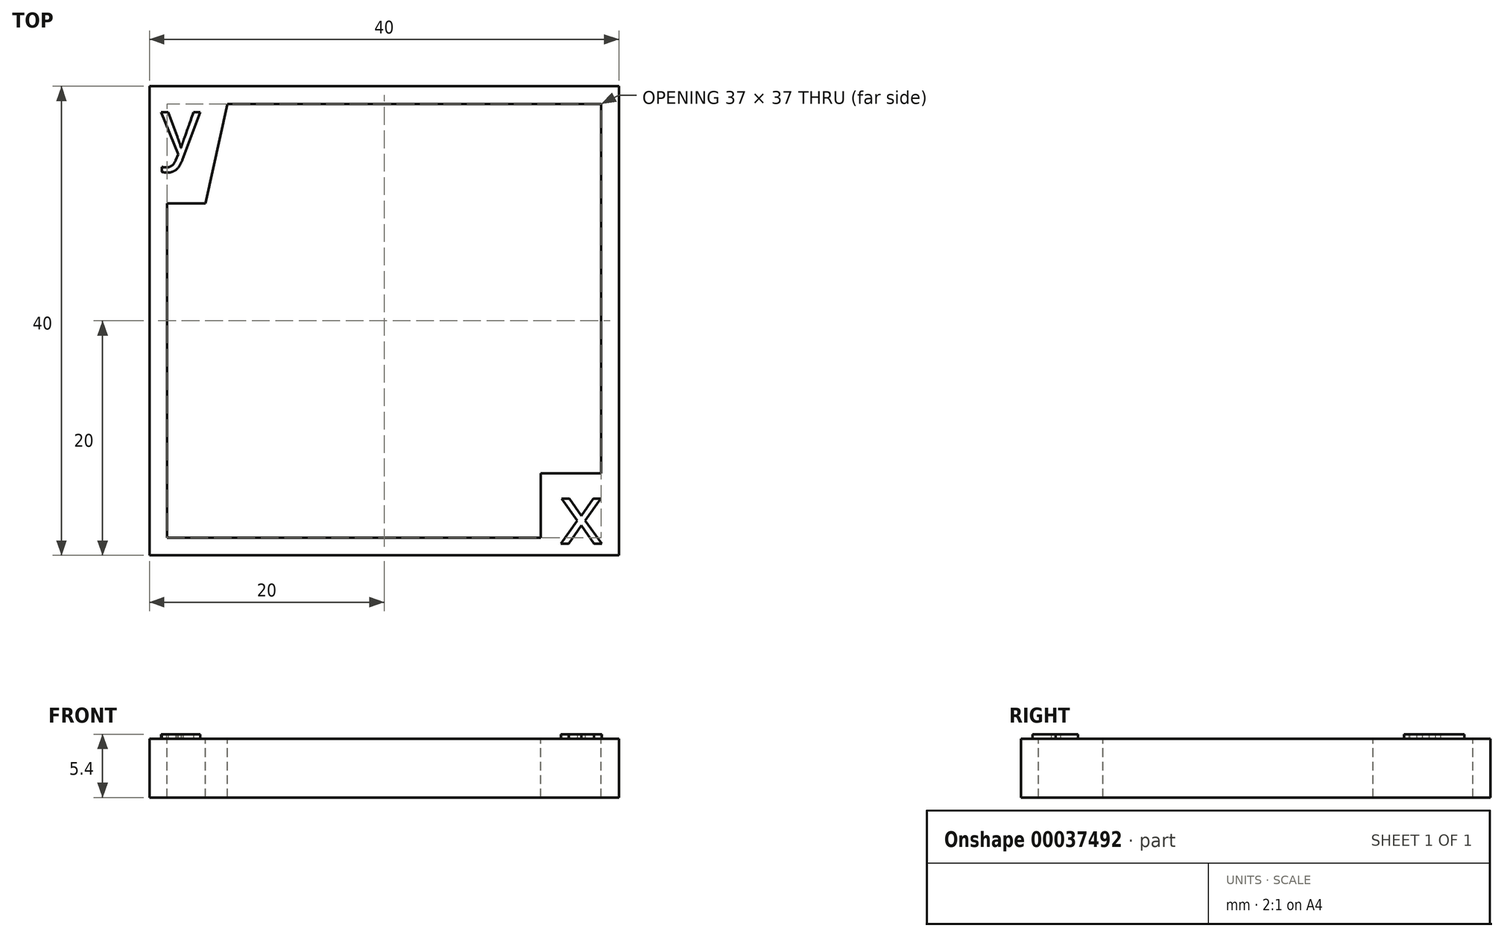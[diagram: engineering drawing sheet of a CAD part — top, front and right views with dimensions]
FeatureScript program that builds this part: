
annotation { "Feature Type Name" : "Feature", "Feature Type Description" : "" }
export const myFeature = defineFeature(function(context is Context, id is Id, definition is map)
    precondition{}
    {
        {
            var Q0;
            Q0=qCreatedBy(makeId("Top.planeOp"),FACE);
            var sketch = newSketch(context, id + "F0", { "sketchPlane" : qUnion([Q0])});
            skLineSegment(sketch, "E0.bottom", {"start": v(20, -20) * mm, "end": v(-20, -20) * mm});
            skLineSegment(sketch, "E0.top", {"start": v(20, 20) * mm, "end": v(-20, 20) * mm});
            skLineSegment(sketch, "E0.left", {"start": v(20, -20) * mm, "end": v(20, 20) * mm});
            skLineSegment(sketch, "E0.right", {"start": v(-20, -20) * mm, "end": v(-20, 20) * mm});
            skPoint(sketch, "E0.middle", {"position": v(0, 0) * mm});
            skSolve(sketch);
        }
        {
            var Q0;
            Q0=qSketchRegion(id+"F0",true);
            extrude(context, id + "F1", {"entities" : qUnion([Q0]), "depth" : 5 * mm});
        }
        {
            var Q0;
            Q0=makeQuery(id+"F1.opExtrude","CAP_FACE",FACE,{"disambiguationData":[OSD([sQuery(id+"F0.wireOp",EDGE,"E0.bottom"),sQuery(id+"F0.wireOp",EDGE,"E0.top"),sQuery(id+"F0.wireOp",EDGE,"E0.left"),sQuery(id+"F0.wireOp",EDGE,"E0.right")])],"isStart":false});
            var sketch = newSketch(context, id + "F2", { "sketchPlane" : qUnion([Q0])});
            skText(sketch, "E1", { "text": "y\n", "fontName": "OpenSans-Regular.ttf"});
            skText(sketch, "E2", { "text": "x\n", "fontName": "OpenSans-Regular.ttf"});
            const initialGuessF2  = {"E1": [-0.019, 0.01423, 1, 0, 0.00477], "E2": [0.01492, -0.019, 1, 0, 0.00517]};
            skSetInitialGuess(sketch, initialGuessF2);
            skSolve(sketch);
        }
        {
            var Q0;
            Q0 = qSketchRegion(id + "F2", true);
            extrude(context, id + "F3", {"entities" : qUnion([Q0]), "operationType" : NewBodyOperationType.ADD, "depth" : .4 * mm});
        }
        {
            var Q0;
            Q0=makeQuery(id+"F1.opExtrude","CAP_FACE",FACE,{"disambiguationData":[OSD([sQuery(id+"F0.wireOp",EDGE,"E0.bottom"),sQuery(id+"F0.wireOp",EDGE,"E0.top"),sQuery(id+"F0.wireOp",EDGE,"E0.left"),sQuery(id+"F0.wireOp",EDGE,"E0.right")])],"isStart":false});
            var sketch = newSketch(context, id + "F4", { "sketchPlane" : qUnion([Q0])});
            skLineSegment(sketch, "E3", {"start": v(-13.35, 18.5) * mm, "end": v(18.5, 18.5) * mm});
            skLineSegment(sketch, "E4", {"start": v(18.5, 18.5) * mm, "end": v(18.5, -13) * mm});
            skLineSegment(sketch, "E5", {"start": v(18.5, -13) * mm, "end": v(13.35, -13) * mm});
            skLineSegment(sketch, "E6", {"start": v(13.35, -13) * mm, "end": v(13.35, -18.5) * mm});
            skLineSegment(sketch, "E7", {"start": v(13.35, -18.5) * mm, "end": v(-18.5, -18.5) * mm});
            skLineSegment(sketch, "E8", {"start": v(-18.5, -18.5) * mm, "end": v(-18.5, 10) * mm});
            skLineSegment(sketch, "E9", {"start": v(-18.5, 10) * mm, "end": v(-15.24, 10) * mm});
            skLineSegment(sketch, "E10", {"start": v(-15.24, 10) * mm, "end": v(-13.35, 18.5) * mm});
            skSolve(sketch);
        }
        {
            var Q0;
            Q0 = qSketchRegion(id + "F4", true);
            extrude(context, id + "F5", {"entities" : qUnion([Q0]), "operationType" : NewBodyOperationType.REMOVE, "oppositeDirection" : true, "depth" : 25 * mm});
        }
    });
